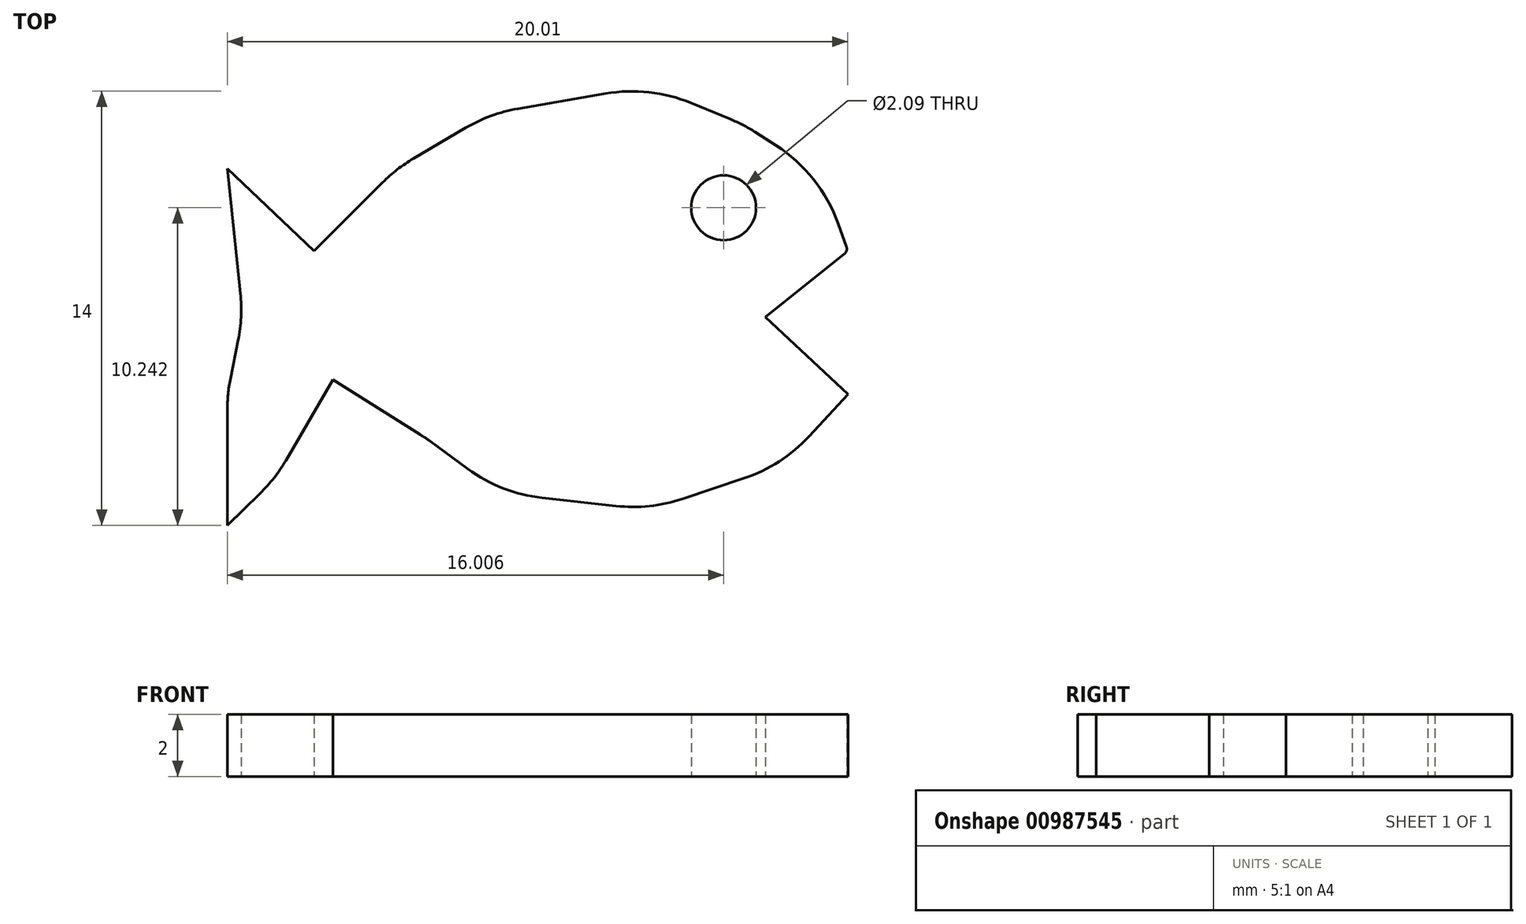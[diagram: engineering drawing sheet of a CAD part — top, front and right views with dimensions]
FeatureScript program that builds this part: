
annotation { "Feature Type Name" : "Feature", "Feature Type Description" : "" }
export const myFeature = defineFeature(function(context is Context, id is Id, definition is map)
    precondition{}
    {
        {
            var Q0;
            Q0=qCreatedBy(makeId("Top.planeOp"),FACE);
            var sketch = newSketch(context, id + "F0", { "sketchPlane" : qUnion([Q0])});
            skPoint(sketch, "E0", {"position": v(0, 7.28) * mm});
            skPoint(sketch, "E1", {"position": v(2.8, 4.62) * mm});
            skPoint(sketch, "E2", {"position": v(5.46, 7.28) * mm});
            skPoint(sketch, "E3", {"position": v(8.48, 9.05) * mm});
            skPoint(sketch, "E4", {"position": v(13.62, 9.94) * mm});
            skPoint(sketch, "E5", {"position": v(16.64, 8.7) * mm});
            skPoint(sketch, "E6", {"position": v(19.13, 7.1) * mm});
            skPoint(sketch, "E7", {"position": v(20.01, 4.62) * mm});
            skPoint(sketch, "E8", {"position": v(17.35, 2.49) * mm});
            skPoint(sketch, "E9", {"position": v(20.01, 0) * mm});
            skPoint(sketch, "E10", {"position": v(17.88, -2.3) * mm});
            skPoint(sketch, "E11", {"position": v(13.62, -3.73) * mm});
            skPoint(sketch, "E12", {"position": v(8.83, -3.2) * mm});
            skPoint(sketch, "E13", {"position": v(6.36, -1.4) * mm});
            skPoint(sketch, "E14", {"position": v(3.4, 0.46) * mm});
            skPoint(sketch, "E15", {"position": v(1.55, -2.72) * mm});
            skPoint(sketch, "E16", {"position": v(0, -4.23) * mm});
            skLineSegment(sketch, "E17", {"start": v(2.8, 4.62) * mm, "end": v(5, 6.83) * mm});
            skLineSegment(sketch, "E18", {"start": v(7.69, 8.6) * mm, "end": v(6, 7.6) * mm});
            skLineSegment(sketch, "E19", {"start": v(9.38, 9.2) * mm, "end": v(12.2, 9.7) * mm});
            skLineSegment(sketch, "E20", {"start": v(16.22, 8.87) * mm, "end": v(14.96, 9.4) * mm});
            skLineSegment(sketch, "E21", {"start": v(17.7, 8.02) * mm, "end": v(17.02, 8.45) * mm});
            skLineSegment(sketch, "E22", {"start": v(19.97, 4.75) * mm, "end": v(19.7, 5.5) * mm});
            skLineSegment(sketch, "E23", {"start": v(19.9, 4.53) * mm, "end": v(17.35, 2.49) * mm});
            skLineSegment(sketch, "E24", {"start": v(17.35, 2.49) * mm, "end": v(20.01, 0) * mm});
            skLineSegment(sketch, "E25", {"start": v(20.01, 0) * mm, "end": v(18.76, -1.36) * mm});
            skLineSegment(sketch, "E26", {"start": v(14.67, -3.38) * mm, "end": v(16.66, -2.71) * mm});
            skLineSegment(sketch, "E27", {"start": v(12.53, -3.6) * mm, "end": v(10.15, -3.34) * mm});
            skLineSegment(sketch, "E28", {"start": v(7.76, -2.41) * mm, "end": v(6.5, -1.5) * mm});
            skLineSegment(sketch, "E29", {"start": v(6.21, -1.3) * mm, "end": v(3.4, 0.46) * mm});
            skLineSegment(sketch, "E30", {"start": v(3.4, 0.46) * mm, "end": v(1.9, -2.13) * mm});
            skLineSegment(sketch, "E31", {"start": v(1.06, -3.2) * mm, "end": v(0, -4.23) * mm});
            skLineSegment(sketch, "E32", {"start": v(0, -4.23) * mm, "end": v(0, -0.5) * mm});
            skLineSegment(sketch, "E33", {"start": v(0.1, 0.5) * mm, "end": v(0.35, 1.73) * mm});
            skLineSegment(sketch, "E34", {"start": v(0, 7.28) * mm, "end": v(0.42, 3.25) * mm});
            skLineSegment(sketch, "E35", {"start": v(0, 7.28) * mm, "end": v(2.8, 4.62) * mm});
            skArc(sketch, "E36.filletArc", {"start": v(6, 7.6) * mm, "mid": v(5.48, 7.25) * mm, "end": v(5, 6.83) * mm});
            skArc(sketch, "E37.filletArc", {"start": v(9.38, 9.2) * mm, "mid": v(8.5, 8.98) * mm, "end": v(7.69, 8.6) * mm});
            skArc(sketch, "E38.filletArc", {"start": v(14.96, 9.4) * mm, "mid": v(13.6, 9.74) * mm, "end": v(12.2, 9.7) * mm});
            skArc(sketch, "E39.filletArc", {"start": v(17.02, 8.45) * mm, "mid": v(16.63, 8.68) * mm, "end": v(16.22, 8.87) * mm});
            skArc(sketch, "E40.filletArc", {"start": v(19.7, 5.5) * mm, "mid": v(18.9, 6.93) * mm, "end": v(17.7, 8.02) * mm});
            skArc(sketch, "E41.filletArc", {"start": v(19.9, 4.53) * mm, "mid": v(19.97, 4.63) * mm, "end": v(19.97, 4.75) * mm});
            skArc(sketch, "E42.filletArc", {"start": v(16.66, -2.71) * mm, "mid": v(17.8, -2.17) * mm, "end": v(18.76, -1.36) * mm});
            skArc(sketch, "E43.filletArc", {"start": v(12.53, -3.6) * mm, "mid": v(13.61, -3.6) * mm, "end": v(14.67, -3.38) * mm});
            skArc(sketch, "E44.filletArc", {"start": v(7.76, -2.41) * mm, "mid": v(8.9, -3.03) * mm, "end": v(10.15, -3.34) * mm});
            skArc(sketch, "E45.filletArc", {"start": v(6.5, -1.5) * mm, "mid": v(6.36, -1.4) * mm, "end": v(6.21, -1.3) * mm});
            skArc(sketch, "E46.filletArc", {"start": v(1.06, -3.2) * mm, "mid": v(1.51, -2.7) * mm, "end": v(1.9, -2.13) * mm});
            skPoint(sketch, "E47.visualSharp", {"position": v(0, 0) * mm});
            skArc(sketch, "E47.filletArc", {"start": v(0.1, 0.5) * mm, "mid": v(0.03, 0) * mm, "end": v(0, -0.5) * mm});
            skArc(sketch, "E48.filletArc", {"start": v(0.35, 1.73) * mm, "mid": v(0.45, 2.49) * mm, "end": v(0.42, 3.25) * mm});
            skCircle(sketch, "E49", {"center": v(16, 6.01) * mm, "radius": 1.04 * mm});
            skSolve(sketch);
        }
        {
            var Q0;
            Q0 = qSketchRegion(id + "F0", true);
            extrude(context, id + "F1", {"entities" : qUnion([Q0]), "depth" : 2 * mm, "offsetDistance" : 25 * mm});
        }
    });
